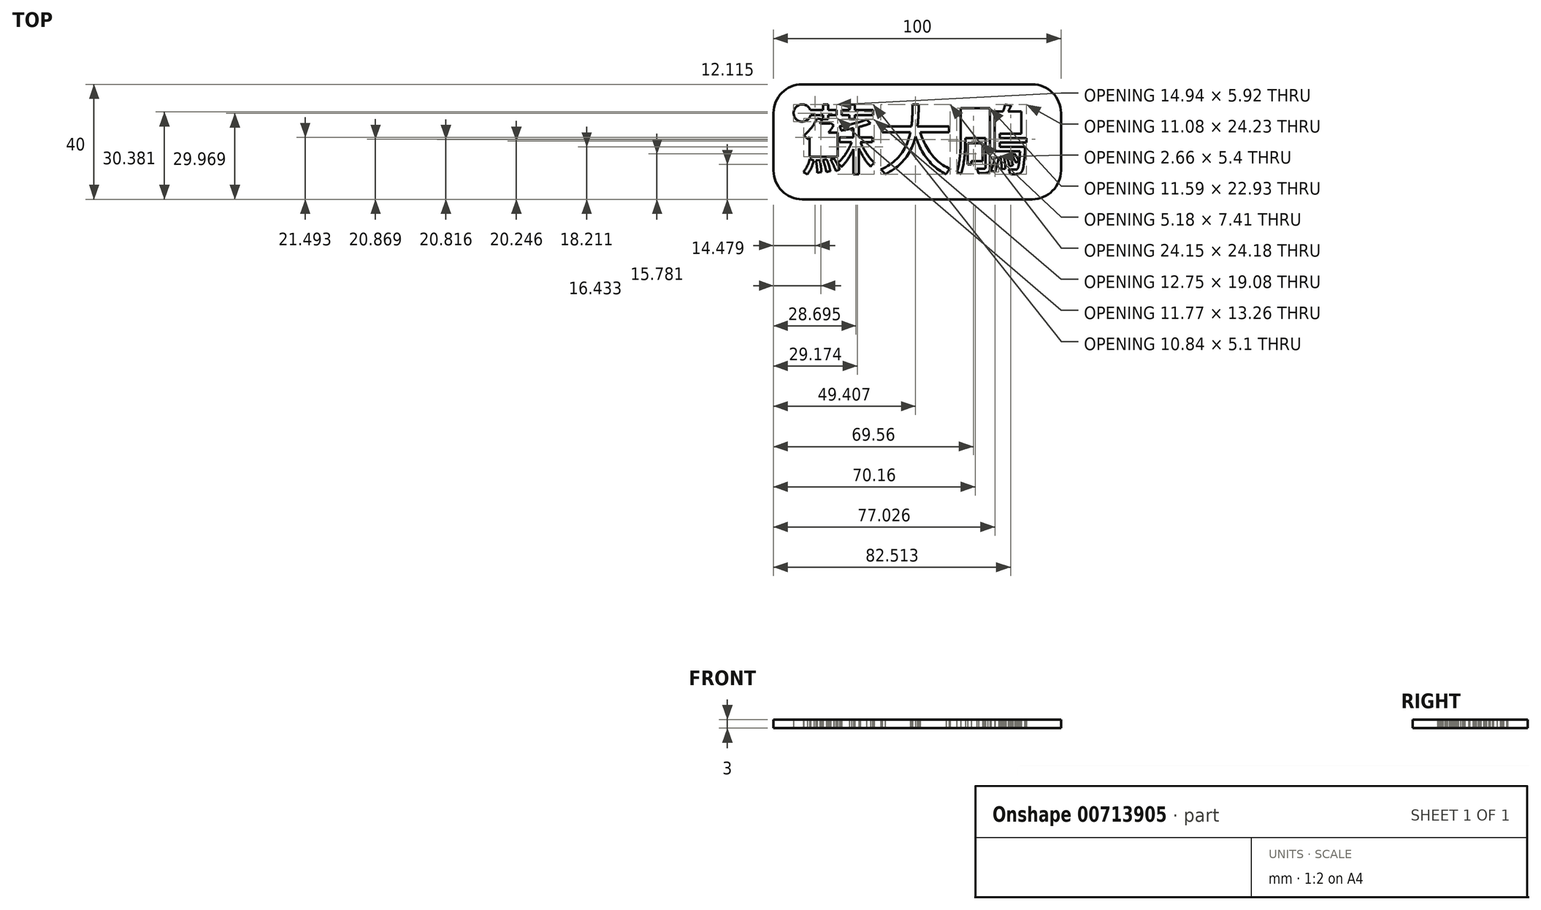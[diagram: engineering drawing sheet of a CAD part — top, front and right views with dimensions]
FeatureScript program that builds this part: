
annotation { "Feature Type Name" : "Feature", "Feature Type Description" : "" }
export const myFeature = defineFeature(function(context is Context, id is Id, definition is map)
    precondition{}
    {
        {
            var Q0;
            Q0=qCreatedBy(makeId("Top.planeOp"),FACE);
            var sketch = newSketch(context, id + "F0", { "sketchPlane" : qUnion([Q0])});
            skLineSegment(sketch, "E0.bottom", {"start": v(10, 0) * mm, "end": v(90, 0) * mm});
            skLineSegment(sketch, "E0.top", {"start": v(10, 40) * mm, "end": v(90, 40) * mm});
            skLineSegment(sketch, "E0.left", {"start": v(0, 10) * mm, "end": v(0, 30) * mm});
            skLineSegment(sketch, "E0.right", {"start": v(100, 10) * mm, "end": v(100, 30) * mm});
            skPoint(sketch, "E1.visualSharp", {"position": v(0, 40) * mm});
            skArc(sketch, "E1.filletArc", {"start": v(10, 40) * mm, "mid": v(2.93, 37.07) * mm, "end": v(0, 30) * mm});
            skPoint(sketch, "E2.visualSharp", {"position": v(0, 0) * mm});
            skArc(sketch, "E2.filletArc", {"start": v(0, 10) * mm, "mid": v(2.93, 2.93) * mm, "end": v(10, 0) * mm});
            skPoint(sketch, "E3.visualSharp", {"position": v(100, 0) * mm});
            skArc(sketch, "E3.filletArc", {"start": v(90, 0) * mm, "mid": v(97.07, 2.93) * mm, "end": v(100, 10) * mm});
            skPoint(sketch, "E4.visualSharp", {"position": v(100, 40) * mm});
            skArc(sketch, "E4.filletArc", {"start": v(100, 30) * mm, "mid": v(97.07, 37.07) * mm, "end": v(90, 40) * mm});
            skCircle(sketch, "E5", {"center": v(10, 30) * mm, "radius": 3 * mm});
            skText(sketch, "E6", { "text": "蘇大鵰\n", "fontName": "NotoSansCJKtc-Regular.otf"});
            const initialGuessF0  = {"E6": [0.00954, 0.01072, 1, 0, 0.01913]};
            skSetInitialGuess(sketch, initialGuessF0);
            skSolve(sketch);
        }
        {
            var Q0;
            Q0 = qSketchRegion(id + "F0", true);
            extrude(context, id + "F1", {"entities" : qUnion([Q0]), "depth" : 3 * mm, "offsetDistance" : 25 * mm});
        }
    });
